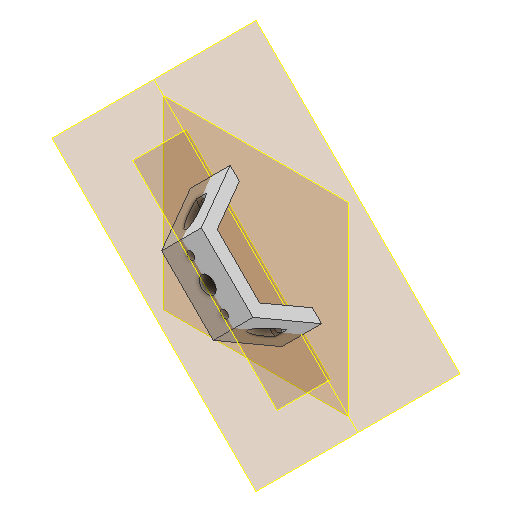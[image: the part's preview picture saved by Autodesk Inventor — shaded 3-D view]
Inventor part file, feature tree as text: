
AUTODESK INVENTOR PART (.ipt)
format: ipt  version: 2022 (Build 260153000, 153)  size: 164,352 bytes
history: native  units: in
note: dims shown in document units (in); Inventor stores cm internally (conversion verified against a paired STEP export)
features: reference x8, other x6, plane x4, sketch x3, extrude x2, hole x1, projected_geometry x1
ambient origin geometry x8: Origin, YZ Plane, XZ Plane, XY Plane, X Axis, Y Axis, Z Axis, Center Point
bodies: Solid1 (feature_tree)
feature tree (25):
  plane  "Work Plane1"
  other  "Work Axis1"
  plane  "Work Plane2"
  plane  "Work Plane3"
  extrude  "Extrusion1"  Depth=0.7874in
  hole  "Hole1"  [1 undecoded]
  extrude  "Extrusion2"  Depth=0.1575in
  plane  "Arbeitsebene4"
  sketch  "Sketch2"  dims[d0=90.0deg d1=0.7874in]
  sketch  "Sketch3"  dims[d2=60.0deg d3=120.0deg]
  sketch  "Sketch4"  dims[d5=0.1575in d6=0.1575in d7=0.1575in d8=0.7874in d9=0.0in d10=0.1102in d11=0.75in d12=0.2559in d13=0.4724in d14=0.5635in d15=1.0in d16=0.8108in d17=0.1102in d18=0.1102in d19=0.7874in d20=0.0in d24=0.2756in d25=0.2756in d26=0.5in d27=0.0344in]
  reference  "Reference6"
  projected_geometry  "Projected Loop1"
  reference  "Reference7"
  reference  "Reference8"
  reference  "Referenz11"
  reference  "Referenz12"
  reference  "Referenz13"
  reference  "Referenz18"
  reference  "Referenz19"
  other  "Anglerfish_bonne_mamman_v0.iam"
  other  "00_toslink_launcher_v3:3"
  other  "Anglerfish_bonne_mamman_m12large_v0.iam"
  other  "00_bonne_maman_jar:1"
  other  "Anglerfish_Lightplate_Tosslink:1"
note: 1 required parameter value undecoded (feature->parameter linkage not recoverable at this tier; creation-order binding heuristic only, values carry confidence <= 0.55)
